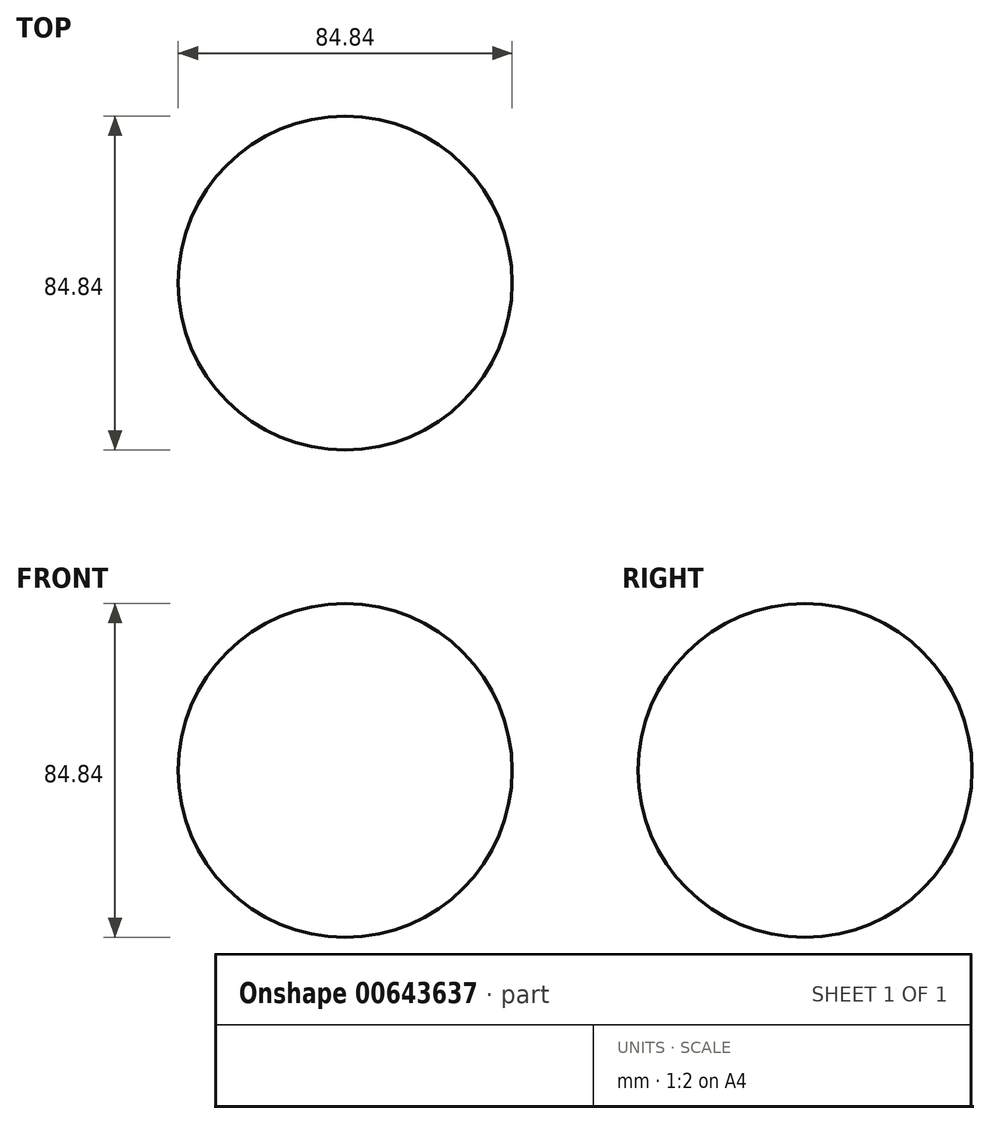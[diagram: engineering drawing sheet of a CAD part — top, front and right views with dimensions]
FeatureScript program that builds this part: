
annotation { "Feature Type Name" : "Feature", "Feature Type Description" : "" }
export const myFeature = defineFeature(function(context is Context, id is Id, definition is map)
    precondition{}
    {
        {
            var Q0;
            Q0=qCreatedBy(makeId("Front.planeOp"),FACE);
            var sketch = newSketch(context, id + "F0", { "sketchPlane" : qUnion([Q0])});
            skArc(sketch, "E0", {"start": v(0, 42.42) * mm, "mid": v(-42.42, 0) * mm, "end": v(0, -42.42) * mm});
            skLineSegment(sketch, "E1", {"start": v(0, 42.42) * mm, "end": v(0, -42.42) * mm});
            skSolve(sketch);
        }
        {
            var Q0;
            Q0=makeQuery(id+"F0.imprint","IMPRINT",FACE,{"disambiguationData":[TD([[makeQuery(id+"F0.imprint","IMPRINT",EDGE,{"derivedFrom":sQuery(id+"F0.wireOp",EDGE,"E0")}),1.0]])]});
            var Q1;
            Q1=sQuery(id+"F0.wireOp",EDGE,"E1");
            revolve(context, id + "F1", {"entities" : qUnion([Q0]), "axis" : qUnion([Q1]), "revolveType" : RevolveType.FULL});
        }
    });
